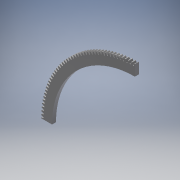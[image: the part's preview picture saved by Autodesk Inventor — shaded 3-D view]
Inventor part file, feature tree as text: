
AUTODESK INVENTOR PART (.ipt)
format: ipt  version: 2017 (Build 210142000, 142)  size: 598,016 bytes
history: native  units: mm (DEFAULTED — no unit token found)
features: sketch x4, extrude x3, plane x3, other x3
ambient origin geometry x8: Origin, YZ Plane, XZ Plane, XY Plane, X Axis, Y Axis, Z Axis, Center Point
bodies: Solid1 (feature_tree)
feature tree (13):
  extrude  "Extrusion1"  Depth=6.35mm TaperAngle=0.0deg
  plane  "Work Plane1"
  plane  "Work Plane2"
  plane  "Work Plane3"
  other  "Spur Gear"
  extrude  "Extrusion2"  Depth=76.2mm TaperAngle=0.0deg
  extrude  "Extrusion3"  TaperAngle=0.0deg  [1 undecoded]
  sketch  "Sketch1"  dims[d0=301.413333mm d1=6.35mm d2=0.0mm]
  sketch  "Sketch2"  dims[d3=298.026667mm d4=76.2mm d5=0.0mm]
  other  "Srf1"
  sketch  "Sketch3"  dims[d6=0.0mm d7=0.1785mm d9=0.0mm]
  sketch  "Sketch4"  dims[d14=0.0mm d15=161.713333mm d16=0.0mm d17=0.0mm d18=0.0mm d19=161.713333mm d20=266.421792mm d21=25.4mm d22=0.0mm d23=0.0mm d24=0.0mm]
  other  "Pitch Diameter"
note: 1 required parameter value undecoded (feature->parameter linkage not recoverable at this tier; creation-order binding heuristic only, values carry confidence <= 0.55)
